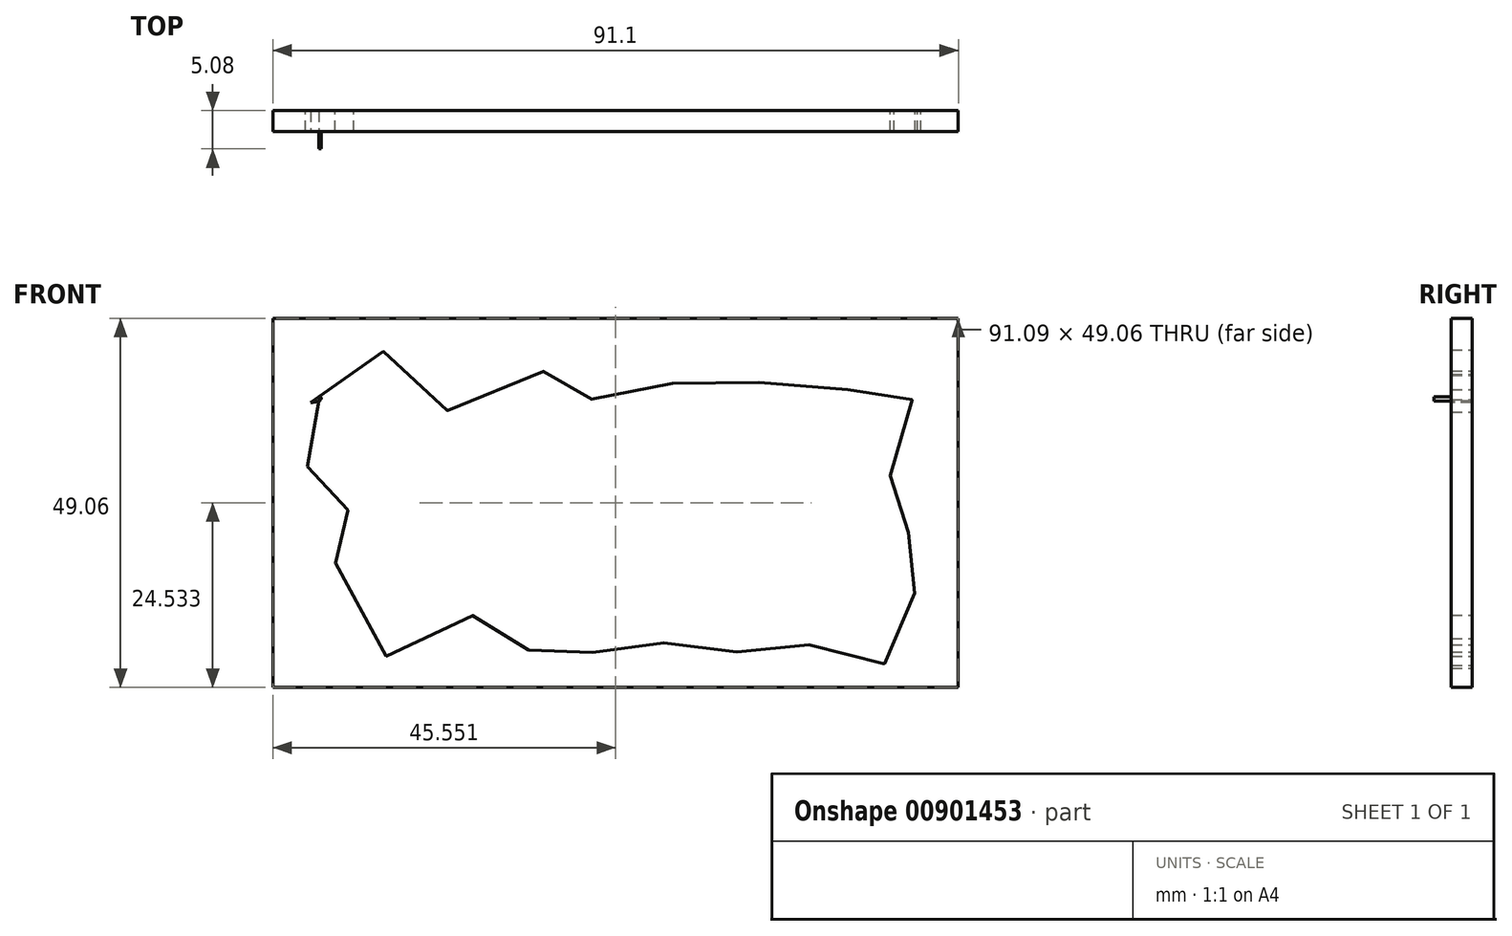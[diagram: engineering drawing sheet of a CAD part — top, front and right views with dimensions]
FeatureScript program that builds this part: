
annotation { "Feature Type Name" : "Feature", "Feature Type Description" : "" }
export const myFeature = defineFeature(function(context is Context, id is Id, definition is map)
    precondition{}
    {
        {
            var Q0;
            Q0=qCreatedBy(makeId("Front.planeOp"),FACE);
            var sketch = newSketch(context, id + "F0", { "sketchPlane" : qUnion([Q0])});
            skLineSegment(sketch, "E0.bottom", {"start": v(-47.24, 18.31) * mm, "end": v(43.86, 18.31) * mm});
            skLineSegment(sketch, "E0.top", {"start": v(-47.24, -30.75) * mm, "end": v(43.86, -30.75) * mm});
            skLineSegment(sketch, "E0.left", {"start": v(-47.24, 18.31) * mm, "end": v(-47.24, -30.75) * mm});
            skLineSegment(sketch, "E0.right", {"start": v(43.86, 18.31) * mm, "end": v(43.86, -30.75) * mm});
            skFitSpline(sketch, "E1", {"points": [v(-42.24, 7.1) * mm, v(-33.18, 14.12) * mm, v(-31.42, 12.23) * mm, v(-22.37, 5.88) * mm, v(-11.15, 11.29) * mm, v(-9.4, 9.93) * mm, v(-5.34, 7.5) * mm, v(3.18, 10.74) * mm, v(10.07, 7.5) * mm, v(21.29, 10.88) * mm, v(29.67, 8.85) * mm, v(35.61, 10.6) * mm, v(37.77, 0) * mm, v(34.8, -2.77) * mm, v(38.86, -7.23) * mm, v(35.34, -12.9) * mm, v(37.91, -17.37) * mm, v(36.29, -23.18) * mm, v(32.9, -28.18) * mm, v(24.8, -25.2) * mm, v(21.15, -25.75) * mm, v(13.58, -26.02) * mm, v(10.6, -25.88) * mm, v(0, -24.26) * mm, v(-3.58, -25.48) * mm, v(-10.34, -27.77) * mm, v(-13.58, -25.34) * mm, v(-17.64, -21.83) * mm, v(-23.31, -21.96) * mm, v(-33.31, -26.29) * mm, v(-38.86, -13.85) * mm, v(-36.96, -12.37) * mm, v(-37.5, -6.7) * mm, v(-41.56, -2.23) * mm, v(-42.5, -1.69) * mm, v(-42.78, 2.5) * mm, v(-40.88, 7.9) * mm], "startDerivative": vector(299.31, 280) * mm, "endDerivative": vector(90.41, 194.84) * mm});
            skFitSpline(sketch, "E2", {"points": [v(-42.24, 7.1) * mm, v(-40.88, 7.48) * mm, v(-40.88, 7.9) * mm], "startDerivative": vector(2.77, 0.41) * mm, "endDerivative": vector(-0.37, 1.3) * mm});
            skCircle(sketch, "E3", {"center": v(-35.35, 5.53) * mm, "radius": 0.61 * mm});
            skCircle(sketch, "E4", {"center": v(6.31, 2.38) * mm, "radius": 1.26 * mm});
            skCircle(sketch, "E5", {"center": v(30.2, -21.42) * mm, "radius": 1.88 * mm});
            skCircle(sketch, "E6", {"center": v(11.1, -12.44) * mm, "radius": 0.67 * mm});
            skCircle(sketch, "E7", {"center": v(10.71, -20.94) * mm, "radius": 0.96 * mm});
            skCircle(sketch, "E8", {"center": v(27.34, -8.13) * mm, "radius": 0.64 * mm});
            skCircle(sketch, "E9", {"center": v(29.15, -0.68) * mm, "radius": 1.22 * mm});
            skCircle(sketch, "E10", {"center": v(-24.17, 0) * mm, "radius": 3.4 * mm});
            skCircle(sketch, "E11", {"center": v(-23.79, -11.48) * mm, "radius": 0.6 * mm});
            skCircle(sketch, "E12", {"center": v(-10.12, -5.94) * mm, "radius": 0.98 * mm});
            skCircle(sketch, "E13", {"center": v(-7.07, -14.44) * mm, "radius": 1.07 * mm});
            skCircle(sketch, "E14", {"center": v(2.2, -5.55) * mm, "radius": 1.57 * mm});
            skCircle(sketch, "E15", {"center": v(17.88, -0.78) * mm, "radius": 1.26 * mm});
            skCircle(sketch, "E16", {"center": v(-16.9, -15.59) * mm, "radius": 1.54 * mm});
            skCircle(sketch, "E17", {"center": v(-7.73, 1.04) * mm, "radius": 1.02 * mm});
            skCircle(sketch, "E18", {"center": v(-31.43, -17.21) * mm, "radius": 1.03 * mm});
            skSolve(sketch);
        }
        {
            var Q0;
            Q0=makeQuery(id+"F0.imprint","IMPRINT",FACE,{"disambiguationData":[TD([[makeQuery(id+"F0.imprint","IMPRINT",EDGE,{"derivedFrom":sQuery(id+"F0.wireOp",EDGE,"E1")}),-1.0]])]});
            extrude(context, id + "F1", {"entities" : qUnion([Q0]), "depth" : 2.3 * mm, "offsetDistance" : 25.4 * mm});
        }
        {
            var Q0;
            Q0 = qSketchRegion(id + "F0", true);
            extrude(context, id + "F2", {"entities" : qUnion([Q0]), "oppositeDirection" : true, "depth" : 2.8 * mm, "offsetDistance" : 25.4 * mm});
        }
    });
